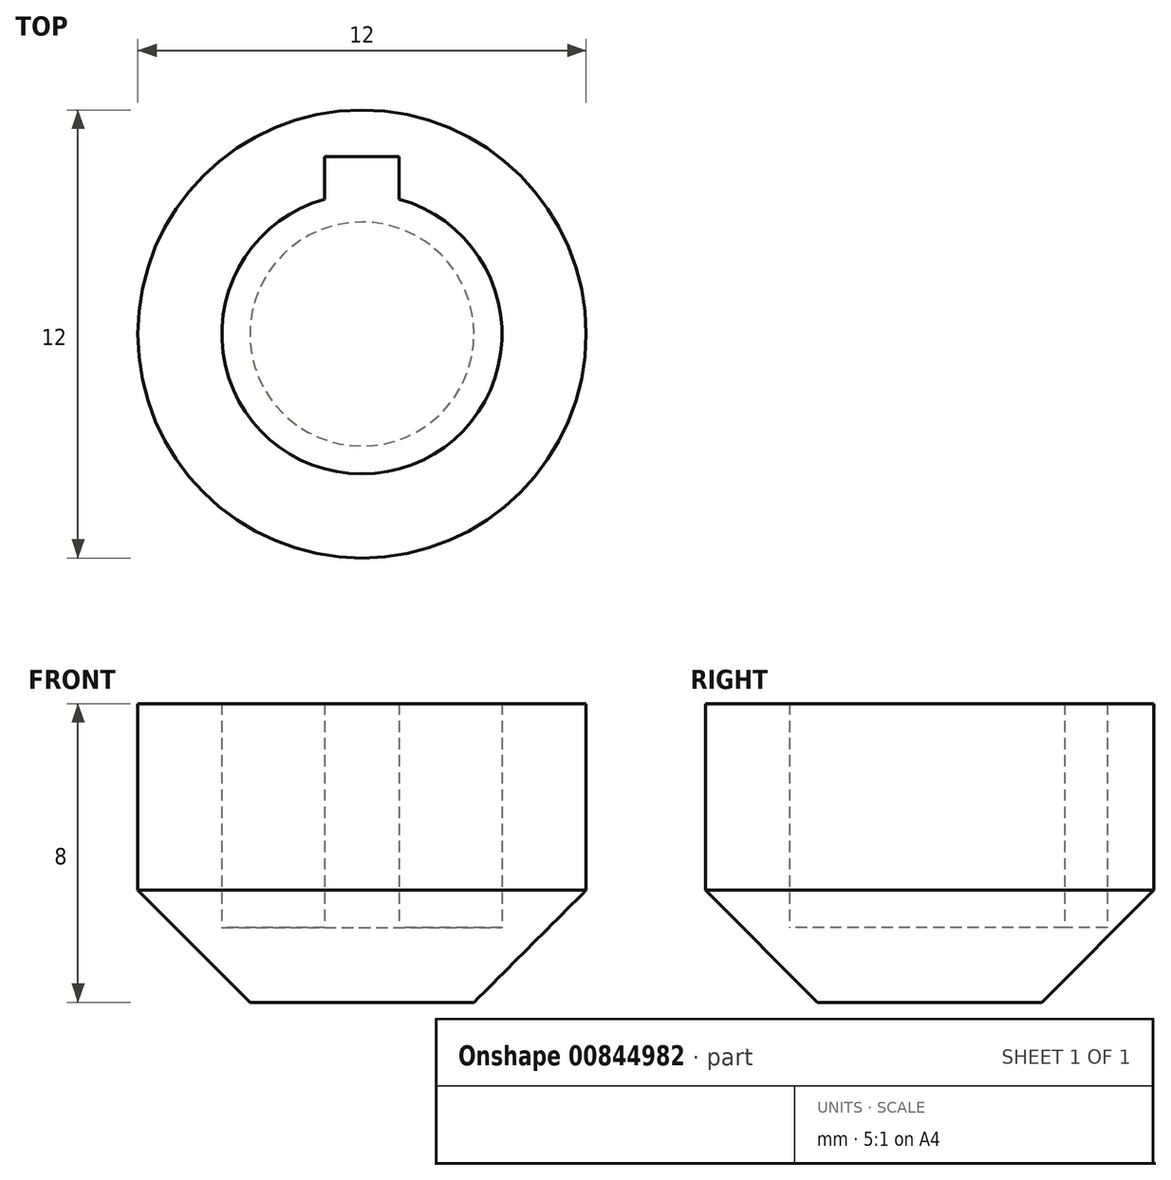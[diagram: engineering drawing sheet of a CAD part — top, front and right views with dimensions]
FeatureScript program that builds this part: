
annotation { "Feature Type Name" : "Feature", "Feature Type Description" : "" }
export const myFeature = defineFeature(function(context is Context, id is Id, definition is map)
    precondition{}
    {
        {
            var Q0;
            Q0=qCreatedBy(makeId("Top.planeOp"),FACE);
            var sketch = newSketch(context, id + "F0", { "sketchPlane" : qUnion([Q0])});
            skCircle(sketch, "E0", {"center": v(0, 0) * mm, "radius": 6 * mm});
            skCircle(sketch, "E1", {"center": v(0, 0) * mm, "radius": 3.75 * mm});
            skLineSegment(sketch, "E2.bottom", {"start": v(-1, 4.75) * mm, "end": v(1, 4.75) * mm});
            skLineSegment(sketch, "E2.top", {"start": v(-1, 2.75) * mm, "end": v(1, 2.75) * mm});
            skLineSegment(sketch, "E2.left", {"start": v(-1, 4.75) * mm, "end": v(-1, 2.75) * mm});
            skLineSegment(sketch, "E2.right", {"start": v(1, 4.75) * mm, "end": v(1, 2.75) * mm});
            skPoint(sketch, "E2.middle", {"position": v(0, 3.75) * mm});
            skSolve(sketch);
        }
        {
            var Q0;
            Q0=makeQuery(id+"F0.imprint","IMPRINT",FACE,{"disambiguationData":[TD([[makeQuery(id+"F0.imprint","IMPRINT",EDGE,{"derivedFrom":sQuery(id+"F0.wireOp",EDGE,"E0")}),1.0]])]});
            extrude(context, id + "F1", {"entities" : qUnion([Q0]), "depth" : 8 * mm, "offsetDistance" : 25 * mm});
        }
        {
            var Q0;
            {var subQ5=sQuery(id+"F0.wireOp",EDGE,"E2.top");Q0=makeQuery(id+"F0.imprint","IMPRINT",FACE,{"disambiguationData":[TD([[makeQuery(id+"F0.imprint","IMPRINT",EDGE,{"derivedFrom":subQ5}),-1.0]])]});}
            var Q1;
            {var subQ5=sQuery(id+"F0.wireOp",EDGE,"E2.top");Q1=makeQuery(id+"F0.imprint","IMPRINT",FACE,{"disambiguationData":[TD([[makeQuery(id+"F0.imprint","IMPRINT",EDGE,{"derivedFrom":subQ5}),1.0]])]});}
            var Q2;
            {var subQ5=sQuery(id+"F0.wireOp",EDGE,"E2.bottom");Q2=makeQuery(id+"F0.imprint","IMPRINT",FACE,{"disambiguationData":[TD([[makeQuery(id+"F0.imprint","IMPRINT",EDGE,{"derivedFrom":subQ5}),-1.0]])]});}
            extrude(context, id + "F2", {"entities" : qUnion([Q0, Q1, Q2]), "operationType" : NewBodyOperationType.ADD, "depth" : 2 * mm, "offsetDistance" : 25 * mm});
        }
        {
            var Q0;
            Q0=makeQuery(id+"F1.opExtrude","CAP_EDGE",EDGE,{"disambiguationData":[OSD([sQuery(id+"F0.wireOp",EDGE,"E0")])],"isStart":true});
            chamfer(context, id + "F3", {"entities" : qUnion([Q0]), "width" : 3 * mm, "tangentPropagation" : true});
        }
    });
